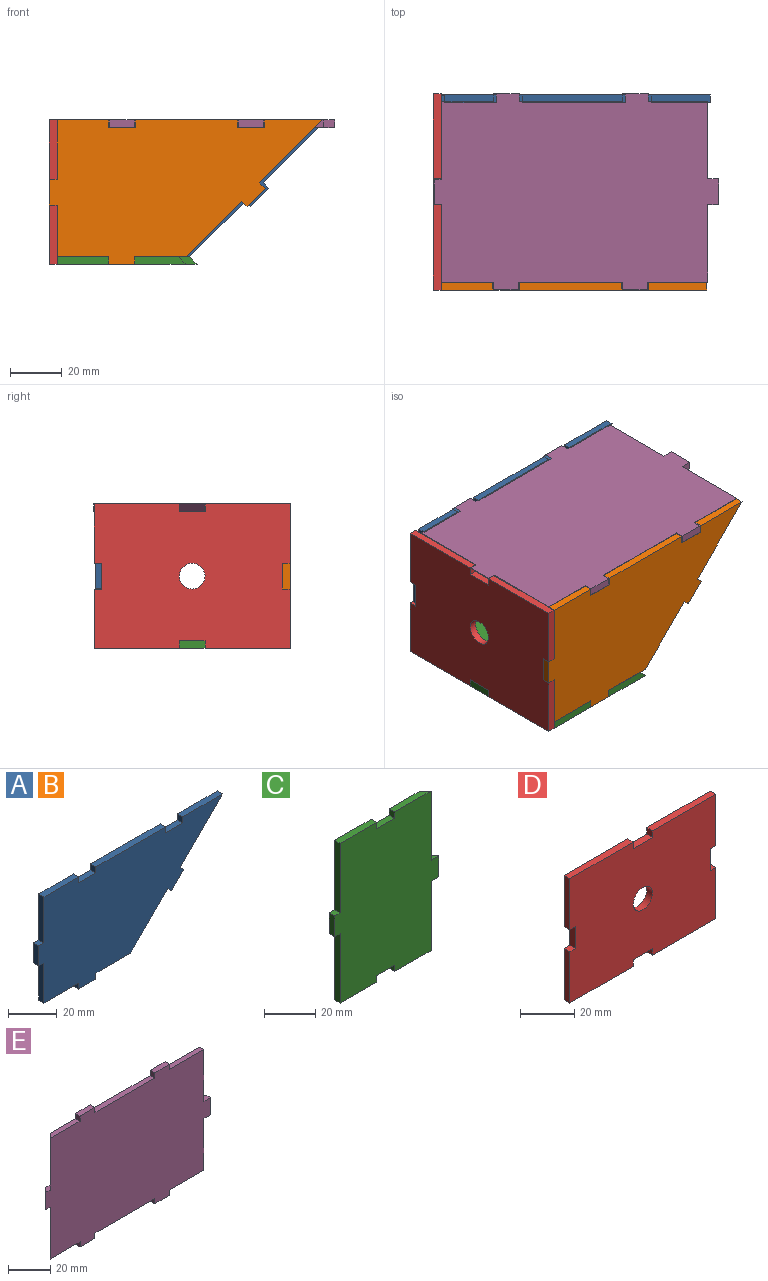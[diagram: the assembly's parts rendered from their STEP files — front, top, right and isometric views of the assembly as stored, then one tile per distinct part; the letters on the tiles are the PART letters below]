
ASSEMBLY  parts=5 mates=4
PART A: 26 faces, bbox 106x3x56 mm
  f0: plane 3x3mm, normal (0,0,1), area 9mm2, adj f1,f23,f24,f25
  f1: plane 10x3mm, normal (-1,0,0), area 30mm2, adj f0,f2,f24,f25
  f2: plane 3x3mm, normal (0,0,-1), area 9mm2, adj f1,f3,f24,f25
  f3: plane 20x3mm, normal (-1,0,0), area 60mm2, adj f2,f4,f24,f25
  f4: plane 20x3mm, normal (0,0,-1), area 60mm2, adj f3,f5,f24,f25
  f5: plane 3x3mm, normal (-1,0,0), area 9mm2, adj f4,f6,f24,f25
  f6: plane 10x3mm, normal (0,0,-1), area 30mm2, adj f5,f7,f24,f25
  f7: plane 3x3mm, normal (1,0,0), area 9mm2, adj f6,f8,f24,f25
  f8: plane 20x3mm, normal (0,0,-1), area 60mm2, adj f7,f9,f24,f25
  f9: plane 21.46x21.46mm, normal (0.71,0,-0.71), area 91.1mm2, adj f8,f10,f24,f25
  f10: plane 3x2.12mm, normal (-0.71,0,-0.71), area 9mm2, adj f9,f11,f24,f25
  f11: plane 7.07x7.07mm, normal (0.71,0,-0.71), area 30mm2, adj f10,f12,f24,f25
  f12: plane 3x2.12mm, normal (0.71,0,0.71), area 9mm2, adj f11,f13,f24,f25
  f13: plane 24.46x24.46mm, normal (0.71,0,-0.71), area 103.8mm2, adj f12,f14,f24,f25
  f14: plane 23x3mm, normal (0,0,1), area 69mm2, adj f13,f15,f24,f25
  f15: plane 3x3mm, normal (-1,0,0), area 9mm2, adj f14,f16,f24,f25
  f16: plane 10x3mm, normal (0,0,1), area 30mm2, adj f15,f17,f24,f25
  f17: plane 3x3mm, normal (1,0,0), area 9mm2, adj f16,f18,f24,f25
  f18: plane 40x3mm, normal (0,0,1), area 120mm2, adj f17,f19,f24,f25
  f19: plane 3x3mm, normal (-1,0,0), area 9mm2, adj f18,f20,f24,f25
  f20: plane 10x3mm, normal (0,0,1), area 30mm2, adj f19,f21,f24,f25
  f21: plane 3x3mm, normal (1,0,0), area 9mm2, adj f20,f22,f24,f25
  f22: plane 20x3mm, normal (0,0,1), area 60mm2, adj f21,f23,f24,f25
  f23: plane 23x3mm, normal (-1,0,0), area 69mm2, adj f0,f22,f24,f25
  f24: plane 106x56mm, normal (0,-1,0), area 4084.5mm2, adj f0,f1,f2,f3,f4,f5,f6,f7
  f25: plane 106x56mm, normal (0,1,0), area 4084.5mm2, adj f0,f1,f2,f3,f4,f5,f6,f7
PART B: same geometry as A
PART C: 22 faces, bbox 57.2x3x76 mm
  f0: plane 3x3mm, normal (0,0,-1), area 9mm2, adj f1,f16,f17,f18
  f1: plane 33x3mm, normal (-1,0,0), area 99mm2, adj f0,f2,f17,f18
  f2: plane 20x3mm, normal (0,0,-1), area 60mm2, adj f1,f3,f17,f18
  f3: plane 3x3mm, normal (1,0,0), area 9mm2, adj f2,f4,f17,f18
  f4: plane 10x3mm, normal (0,0,-1), area 30mm2, adj f3,f5,f17,f18
  f5: plane 3x3mm, normal (-1,0,0), area 9mm2, adj f4,f6,f17,f18
  f6: plane 20x3mm, normal (0,0,-1), area 55.5mm2, adj f5,f17,f18,f19
  f7: plane 7.24x3mm, normal (0,0,-1), area 12.7mm2, adj f17,f18,f19,f20
  f8: plane 7.24x3mm, normal (0,0,1), area 12.7mm2, adj f17,f18,f20,f21
  f9: plane 20x3mm, normal (0,0,1), area 55.5mm2, adj f10,f17,f18,f21
  f10: plane 3x3mm, normal (-1,0,0), area 9mm2, adj f9,f11,f17,f18
  f11: plane 10x3mm, normal (0,0,1), area 30mm2, adj f10,f12,f17,f18
  f12: plane 3x3mm, normal (1,0,0), area 9mm2, adj f11,f13,f17,f18
  f13: plane 20x3mm, normal (0,0,1), area 60mm2, adj f12,f14,f17,f18
  f14: plane 33x3mm, normal (-1,0,0), area 99mm2, adj f13,f15,f17,f18
  f15: plane 3x3mm, normal (0,0,1), area 9mm2, adj f14,f16,f17,f18
  f16: plane 10x3mm, normal (-1,0,0), area 30mm2, adj f0,f15,f17,f18
  f17: plane 76x57.24mm, normal (0,-1,0), area 3812.4mm2, adj f0,f1,f2,f3,f4,f5,f6,f7
  f18: plane 76x54.24mm, normal (0,1,0), area 3584.4mm2, adj f0,f1,f2,f3,f4,f5,f6,f7
  f19: plane 33x3mm, normal (0.71,0.71,0), area 140mm2, adj f6,f7,f17,f18
  f20: plane 10x3mm, normal (0.71,0.71,0), area 42.4mm2, adj f7,f8,f17,f18
  f21: plane 33x3mm, normal (0.71,0.71,0), area 140mm2, adj f8,f9,f17,f18
PART D: 23 faces, bbox 76x3x56 mm
  f0: plane 33x3mm, normal (0,0,1), area 99mm2, adj f1,f19,f21,f22
  f1: plane 3x3mm, normal (-1,0,0), area 9mm2, adj f0,f2,f21,f22
  f2: plane 10x3mm, normal (0,0,1), area 30mm2, adj f1,f3,f21,f22
  f3: plane 3x3mm, normal (1,0,0), area 9mm2, adj f2,f4,f21,f22
  f4: plane 33x3mm, normal (0,0,1), area 99mm2, adj f3,f5,f21,f22
  f5: plane 23x3mm, normal (-1,0,0), area 69mm2, adj f4,f6,f21,f22
  f6: plane 3x3mm, normal (0,0,-1), area 9mm2, adj f5,f7,f21,f22
  f7: plane 10x3mm, normal (-1,0,0), area 30mm2, adj f6,f8,f21,f22
  f8: plane 3x3mm, normal (0,0,1), area 9mm2, adj f7,f9,f21,f22
  f9: plane 23x3mm, normal (-1,0,0), area 69mm2, adj f8,f10,f21,f22
  f10: plane 33x3mm, normal (0,0,-1), area 99mm2, adj f9,f11,f21,f22
  f11: plane 3x3mm, normal (1,0,0), area 9mm2, adj f10,f12,f21,f22
  f12: plane 10x3mm, normal (0,0,-1), area 30mm2, adj f11,f13,f21,f22
  f13: plane 3x3mm, normal (-1,0,0), area 9mm2, adj f12,f14,f21,f22
  f14: plane 33x3mm, normal (0,0,-1), area 99mm2, adj f13,f15,f21,f22
  f15: plane 23x3mm, normal (1,0,0), area 69mm2, adj f14,f16,f21,f22
  f16: plane 3x3mm, normal (0,0,1), area 9mm2, adj f15,f17,f21,f22
  f17: plane 10x3mm, normal (1,0,0), area 30mm2, adj f16,f18,f21,f22
  f18: plane 3x3mm, normal (0,0,-1), area 9mm2, adj f17,f19,f21,f22
  f19: plane 23x3mm, normal (1,0,0), area 69mm2, adj f0,f18,f21,f22
  f20: cylinder r=5mm len=10mm, axis (0,1,0), area 94.2mm2, adj f21,f22
  f21: plane 76x56mm, normal (0,-1,0), area 4057.5mm2, adj f0,f1,f2,f3,f4,f5,f6,f7
  f22: plane 76x56mm, normal (0,1,0), area 4057.5mm2, adj f0,f1,f2,f3,f4,f5,f6,f7
PART E: 30 faces, bbox 110.2x3x76 mm
  f0: plane 6x3mm, normal (0,0,-1), area 9mm2, adj f25,f26,f28,f29
  f1: plane 20x3mm, normal (0,0,-1), area 55.5mm2, adj f2,f25,f26,f29
  f2: plane 3x3mm, normal (-1,0,0), area 9mm2, adj f1,f3,f25,f26
  f3: plane 10x3mm, normal (0,0,-1), area 30mm2, adj f2,f4,f25,f26
  f4: plane 3x3mm, normal (1,0,0), area 9mm2, adj f3,f5,f25,f26
  f5: plane 40x3mm, normal (0,0,-1), area 120mm2, adj f4,f6,f25,f26
  f6: plane 3x3mm, normal (-1,0,0), area 9mm2, adj f5,f7,f25,f26
  f7: plane 10x3mm, normal (0,0,-1), area 30mm2, adj f6,f8,f25,f26
  f8: plane 3x3mm, normal (1,0,0), area 9mm2, adj f7,f9,f25,f26
  f9: plane 23x3mm, normal (0,0,-1), area 69mm2, adj f8,f10,f25,f26
  f10: plane 30x3mm, normal (1,0,0), area 90mm2, adj f9,f11,f25,f26
  f11: plane 4.24x3mm, normal (0,0,-1), area 12.7mm2, adj f10,f12,f25,f26
  f12: plane 10x3mm, normal (1,0,0), area 30mm2, adj f11,f13,f25,f26
  f13: plane 4.24x3mm, normal (0,0,1), area 12.7mm2, adj f12,f14,f25,f26
  f14: plane 30x3mm, normal (1,0,0), area 90mm2, adj f13,f15,f25,f26
  f15: plane 23x3mm, normal (0,0,1), area 69mm2, adj f14,f16,f25,f26
  f16: plane 3x3mm, normal (1,0,0), area 9mm2, adj f15,f17,f25,f26
  f17: plane 10x3mm, normal (0,0,1), area 30mm2, adj f16,f18,f25,f26
  f18: plane 3x3mm, normal (-1,0,0), area 9mm2, adj f17,f19,f25,f26
  f19: plane 40x3mm, normal (0,0,1), area 120mm2, adj f18,f20,f25,f26
  f20: plane 3x3mm, normal (1,0,0), area 9mm2, adj f19,f21,f25,f26
  f21: plane 10x3mm, normal (0,0,1), area 30mm2, adj f20,f22,f25,f26
  f22: plane 3x3mm, normal (-1,0,0), area 9mm2, adj f21,f23,f25,f26
  f23: plane 20x3mm, normal (0,0,1), area 55.5mm2, adj f22,f25,f26,f27
  f24: plane 6x3mm, normal (0,0,1), area 9mm2, adj f25,f26,f27,f28
  f25: plane 110.24x76mm, normal (0,-1,0), area 7402.4mm2, adj f0,f1,f2,f3,f4,f5,f6,f7
  f26: plane 107.24x76mm, normal (0,1,0), area 7192.4mm2, adj f0,f1,f2,f3,f4,f5,f6,f7
  f27: plane 30x3mm, normal (-0.71,0.71,0), area 127.3mm2, adj f23,f24,f25,f26
  f28: plane 10x3mm, normal (-0.71,0.71,0), area 42.4mm2, adj f0,f24,f25,f26
  f29: plane 30x3mm, normal (-0.71,0.71,0), area 127.3mm2, adj f0,f1,f25,f26
PLACE A t=(53.14,-1.53,13.36)mm
PLACE B t=(51.74,-74.14,13.28)mm
PLACE C rot(axis=(1,0,0),90deg) t=(37.23,-39.14,-16.21)mm fixed
PLACE D rot(axis=(0,0,-1),90deg) t=(12.11,-39.14,8.79)mm
PLACE E rot(axis=(-1,0,0),90deg) t=(62.38,-39.05,33.82)mm
MATE planar C.f13 <-> B.f24  axis (0,-1,0) through (32.11,-77.14,-19.21)mm
MATE parallel D.f22 <-> C.f14  axis (1,0,0) through (12.11,-60.64,-19.21)mm
MATE parallel E.f25 <-> C.f17  axis (0,0,1) through (42.38,-2.55,36.82)mm
MATE planar D.f12 <-> C.f18  axis (0,0,-1) through (10.61,-39.14,-16.21)mm
